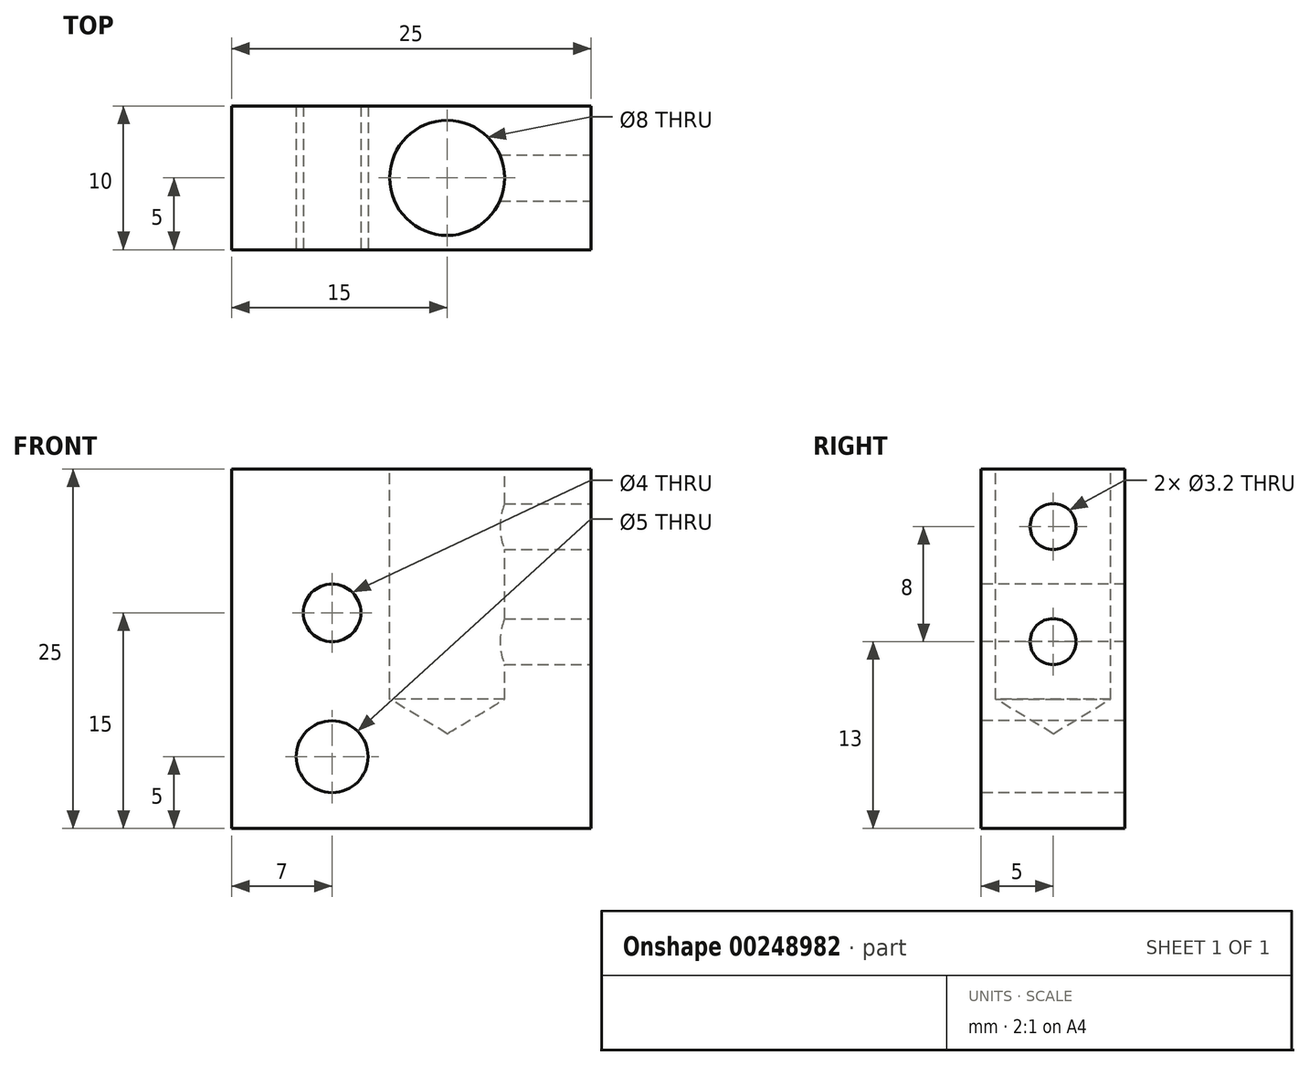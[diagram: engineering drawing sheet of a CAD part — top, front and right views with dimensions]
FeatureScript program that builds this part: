
annotation { "Feature Type Name" : "Feature", "Feature Type Description" : "" }
export const myFeature = defineFeature(function(context is Context, id is Id, definition is map)
    precondition{}
    {
        {
            var Q0;
            Q0=qCreatedBy(makeId("Front.planeOp"),FACE);
            var sketch = newSketch(context, id + "F0", { "sketchPlane" : qUnion([Q0])});
            skLineSegment(sketch, "E0.bottom", {"start": v(12.5, 12.5) * mm, "end": v(-12.5, 12.5) * mm});
            skLineSegment(sketch, "E0.top", {"start": v(12.5, -12.5) * mm, "end": v(-12.5, -12.5) * mm});
            skLineSegment(sketch, "E0.left", {"start": v(12.5, 12.5) * mm, "end": v(12.5, -12.5) * mm});
            skLineSegment(sketch, "E0.right", {"start": v(-12.5, 12.5) * mm, "end": v(-12.5, -12.5) * mm});
            skPoint(sketch, "E0.middle", {"position": v(0, 0) * mm});
            skSolve(sketch);
        }
        {
            var Q0;
            Q0=makeQuery(id+"F0.imprint","IMPRINT",FACE,{"disambiguationData":[TD([[makeQuery(id+"F0.imprint","IMPRINT",EDGE,{"derivedFrom":sQuery(id+"F0.wireOp",EDGE,"E0.bottom")}),1.0]])]});
            extrude(context, id + "F1", {"entities" : qUnion([Q0]), "endBound" : BoundingType.SYMMETRIC, "depth" : 10 * mm});
        }
        {
            var Q0;
            Q0=makeQuery(id+"F1.opExtrude","CAP_FACE",FACE,{"disambiguationData":[OSD([sQuery(id+"F0.wireOp",EDGE,"E0.bottom"),sQuery(id+"F0.wireOp",EDGE,"E0.top"),sQuery(id+"F0.wireOp",EDGE,"E0.left"),sQuery(id+"F0.wireOp",EDGE,"E0.right")])],"isStart":false});
            var sketch = newSketch(context, id + "F2", { "sketchPlane" : qUnion([Q0])});
            skPoint(sketch, "E1", {"position": v(-5.5, 2.5) * mm});
            skPoint(sketch, "E2", {"position": v(-5.5, -7.5) * mm});
            skSolve(sketch);
        }
        {
            var Q0;
            Q0=sQuery(id+"F2.wireOp",VERTEX,"E1");
            var Q1;
            Q1=makeQuery(id+"F1.opExtrude","SWEPT_BODY",BODY,{"disambiguationData":[OSD([sQuery(id+"F0.wireOp",EDGE,"E0.bottom"),sQuery(id+"F0.wireOp",EDGE,"E0.top"),sQuery(id+"F0.wireOp",EDGE,"E0.left"),sQuery(id+"F0.wireOp",EDGE,"E0.right")])]});
            hole(context, id + "F3", {"style" : HoleStyle.SIMPLE, "endStyle" : HoleEndStyle.THROUGH, "holeDiameter" : 4 * mm, "tappedDepth" : 4.2 * mm, "tapClearance" : 3, "startFromSketch" : true, "locations" : qUnion([Q0]), "scope" : qUnion([Q1])});
        }
        {
            var Q0;
            Q0=sQuery(id+"F2.wireOp",VERTEX,"E2");
            var Q1;
            Q1=makeQuery(id+"F1.opExtrude","SWEPT_BODY",BODY,{"disambiguationData":[OSD([sQuery(id+"F0.wireOp",EDGE,"E0.bottom"),sQuery(id+"F0.wireOp",EDGE,"E0.top"),sQuery(id+"F0.wireOp",EDGE,"E0.left"),sQuery(id+"F0.wireOp",EDGE,"E0.right")])]});
            hole(context, id + "F4", {"style" : HoleStyle.SIMPLE, "endStyle" : HoleEndStyle.THROUGH, "holeDiameter" : 5 * mm, "tappedDepth" : 4.2 * mm, "tapClearance" : 3, "startFromSketch" : true, "locations" : qUnion([Q0]), "scope" : qUnion([Q1])});
        }
        {
            var Q0;
            Q0=makeQuery(id+"F1.opExtrude","SWEPT_FACE",FACE,{"disambiguationData":[OSD([sQuery(id+"F0.wireOp",EDGE,"E0.bottom")])]});
            var sketch = newSketch(context, id + "F5", { "sketchPlane" : qUnion([Q0])});
            skPoint(sketch, "E3", {"position": v(2.5, 0) * mm});
            skSolve(sketch);
        }
        {
            var Q0;
            Q0=sQuery(id+"F5.wireOp",VERTEX,"E3");
            var Q1;
            Q1=makeQuery(id+"F1.opExtrude","SWEPT_BODY",BODY,{"disambiguationData":[OSD([sQuery(id+"F0.wireOp",EDGE,"E0.bottom"),sQuery(id+"F0.wireOp",EDGE,"E0.top"),sQuery(id+"F0.wireOp",EDGE,"E0.left"),sQuery(id+"F0.wireOp",EDGE,"E0.right")])]});
            hole(context, id + "F6", {"style" : HoleStyle.SIMPLE, "endStyle" : HoleEndStyle.BLIND, "holeDiameter" : 8 * mm, "holeDepth" : 16 * mm, "tappedDepth" : 4.2 * mm, "tapClearance" : 3, "startFromSketch" : true, "locations" : qUnion([Q0]), "scope" : qUnion([Q1])});
        }
        {
            var Q0;
            Q0=makeQuery(id+"F1.opExtrude","SWEPT_FACE",FACE,{"disambiguationData":[OSD([sQuery(id+"F0.wireOp",EDGE,"E0.left")])]});
            var sketch = newSketch(context, id + "F7", { "sketchPlane" : qUnion([Q0])});
            skPoint(sketch, "E4", {"position": v(0, 0.5) * mm});
            skPoint(sketch, "E5", {"position": v(0, 8.5) * mm});
            skSolve(sketch);
        }
        {
            var Q0;
            Q0=sQuery(id+"F7.wireOp",VERTEX,"E5");
            var Q1;
            Q1=sQuery(id+"F7.wireOp",VERTEX,"E4");
            var Q2;
            Q2=makeQuery(id+"F1.opExtrude","SWEPT_BODY",BODY,{"disambiguationData":[OSD([sQuery(id+"F0.wireOp",EDGE,"E0.bottom"),sQuery(id+"F0.wireOp",EDGE,"E0.top"),sQuery(id+"F0.wireOp",EDGE,"E0.left"),sQuery(id+"F0.wireOp",EDGE,"E0.right")])]});
            hole(context, id + "F8", {"style" : HoleStyle.SIMPLE, "endStyle" : HoleEndStyle.BLIND, "standardTappedOrClearance" : lookupTablePath({ "standard" : "ISO", "engagement" : "75%", "pitch" : "0.75 mm", "size" : "M4", "type" : "Tapped" }), "standardBlindInLast" : lookupTablePath({ "standard" : "ISO", "engagement" : "75%", "pitch" : "0.75 mm", "size" : "M4", "type" : "Tapped" }), "holeDiameter" : 3.2 * mm, "showTappedDepth" : true, "holeDepth" : 10 * mm, "tappedDepth" : 7.75 * mm, "tapClearance" : 3, "startFromSketch" : true, "locations" : qUnion([Q0, Q1]), "scope" : qUnion([Q2])});
        }
    });
